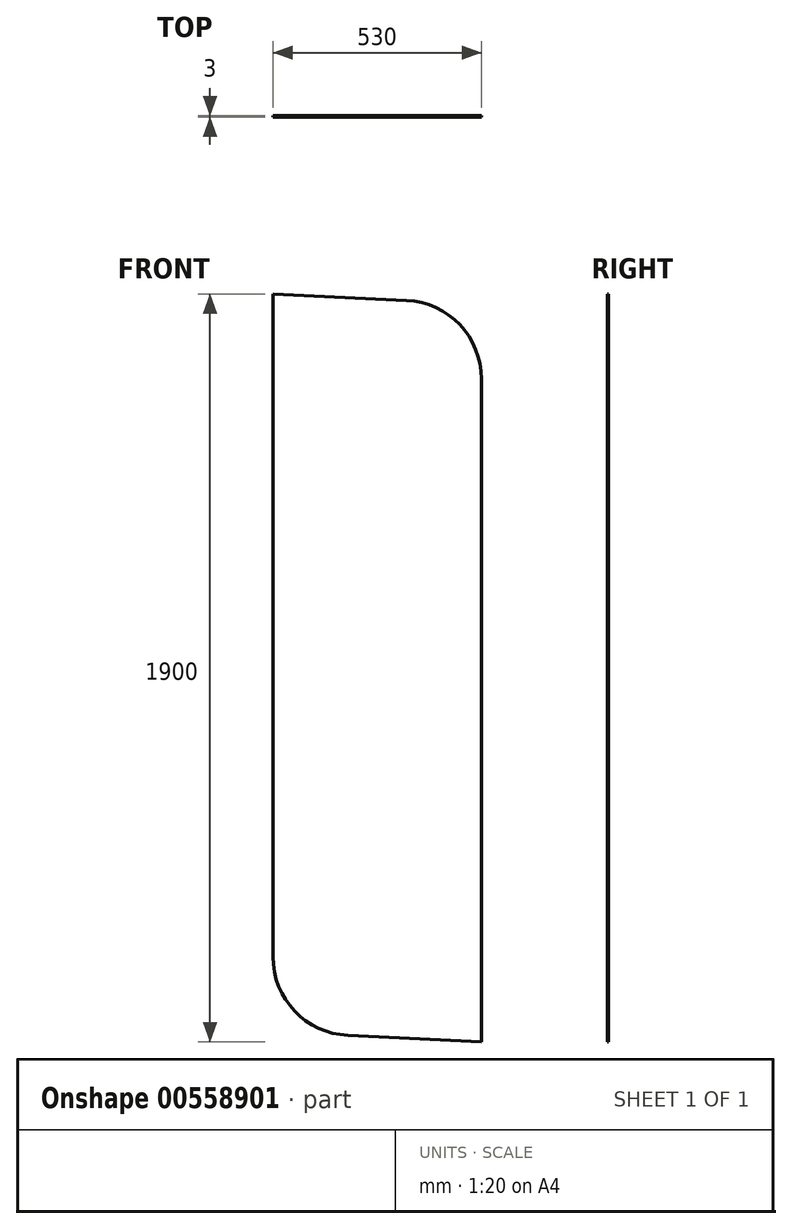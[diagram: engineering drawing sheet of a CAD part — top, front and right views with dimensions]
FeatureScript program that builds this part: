
annotation { "Feature Type Name" : "Feature", "Feature Type Description" : "" }
export const myFeature = defineFeature(function(context is Context, id is Id, definition is map)
    precondition{}
    {
        {
            var Q0;
            Q0=qCreatedBy(makeId("Front.planeOp"),FACE);
            var sketch = newSketch(context, id + "F0", { "sketchPlane" : qUnion([Q0])});
            skLineSegment(sketch, "E0.bottom", {"start": v(0, 0) * mm, "end": v(530, 0) * mm, "construction": true});
            skLineSegment(sketch, "E0.top", {"start": v(0, 1900) * mm, "end": v(530, 1900) * mm, "construction": true});
            skLineSegment(sketch, "E0.left", {"start": v(0, 0) * mm, "end": v(0, 1900) * mm, "construction": true});
            skLineSegment(sketch, "E0.right", {"start": v(530, 0) * mm, "end": v(530, 1900) * mm, "construction": true});
            skLineSegment(sketch, "E1", {"start": v(530, 0) * mm, "end": v(190.4, 16.33) * mm});
            skArc(sketch, "E2", {"start": v(190.4, 16.33) * mm, "mid": v(55.22, 78.12) * mm, "end": v(0, 216.1) * mm});
            skLineSegment(sketch, "E3", {"start": v(0, 1900) * mm, "end": v(0, 216.1) * mm});
            skLineSegment(sketch, "E4", {"start": v(0, 1900) * mm, "end": v(339.6, 1883.67) * mm});
            skArc(sketch, "E5", {"start": v(339.6, 1883.67) * mm, "mid": v(474.78, 1821.88) * mm, "end": v(530, 1683.9) * mm});
            skLineSegment(sketch, "E6", {"start": v(530, 1683.9) * mm, "end": v(530, 0) * mm});
            skSolve(sketch);
        }
        {
            var Q0;
            Q0=makeQuery(id+"F0.imprint","IMPRINT",FACE,{"disambiguationData":[TD([[makeQuery(id+"F0.imprint","IMPRINT",EDGE,{"derivedFrom":sQuery(id+"F0.wireOp",EDGE,"E1")}),-1.0]])]});
            extrude(context, id + "F1", {"entities" : qUnion([Q0]), "depth" : 3 * mm, "offsetDistance" : 25 * mm});
        }
    });
